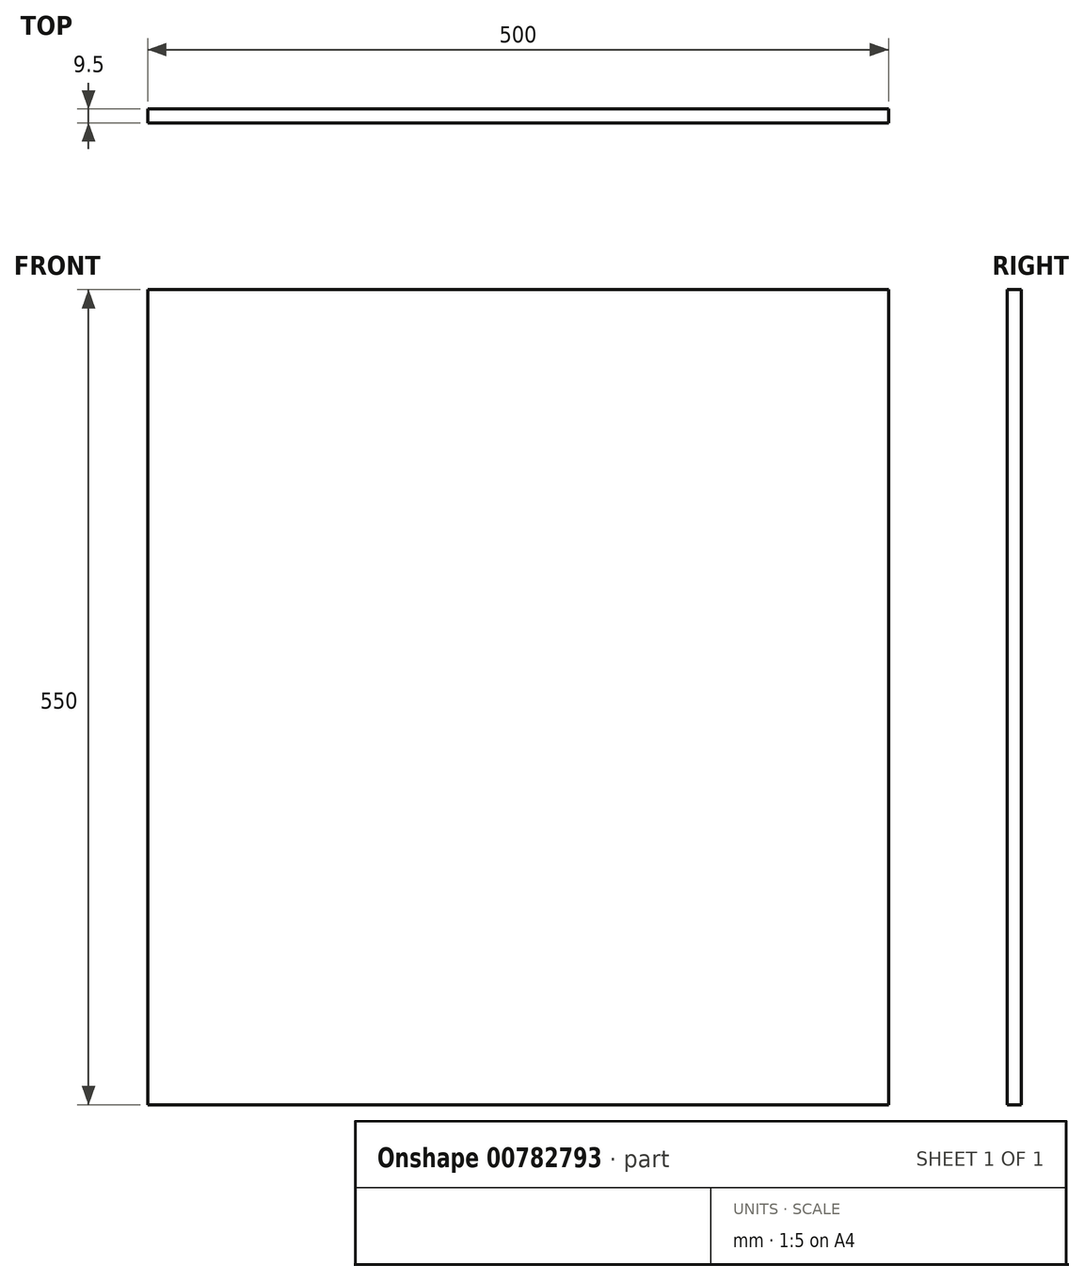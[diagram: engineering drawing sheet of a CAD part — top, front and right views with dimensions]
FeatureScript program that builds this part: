
annotation { "Feature Type Name" : "Feature", "Feature Type Description" : "" }
export const myFeature = defineFeature(function(context is Context, id is Id, definition is map)
    precondition{}
    {
        {
            var Q0;
            Q0=qCreatedBy(makeId("Front.planeOp"),FACE);
            var sketch = newSketch(context, id + "F0", { "sketchPlane" : qUnion([Q0])});
            skLineSegment(sketch, "E0.bottom", {"start": v(572.82, 565.4) * mm, "end": v(72.82, 565.4) * mm});
            skLineSegment(sketch, "E0.top", {"start": v(572.82, 15.4) * mm, "end": v(72.82, 15.4) * mm});
            skLineSegment(sketch, "E0.left", {"start": v(572.82, 565.4) * mm, "end": v(572.82, 15.4) * mm});
            skLineSegment(sketch, "E0.right", {"start": v(72.82, 565.4) * mm, "end": v(72.82, 15.4) * mm});
            skSolve(sketch);
        }
        {
            var Q0;
            Q0 = qSketchRegion(id + "F0", true);
            extrude(context, id + "F1", {"entities" : qUnion([Q0]), "depth" : 9.5 * mm, "offsetDistance" : 25 * mm});
        }
    });
